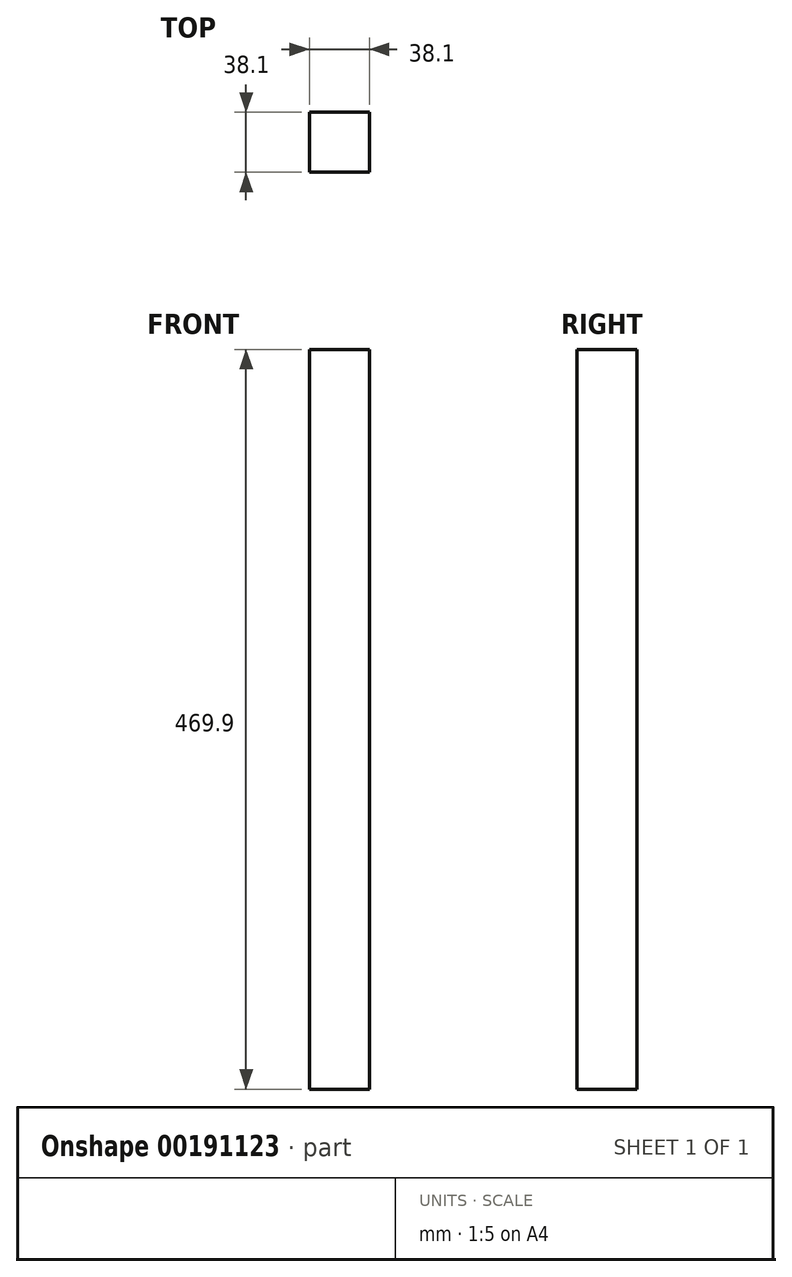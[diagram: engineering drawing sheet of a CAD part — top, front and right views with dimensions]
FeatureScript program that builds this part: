
annotation { "Feature Type Name" : "Feature", "Feature Type Description" : "" }
export const myFeature = defineFeature(function(context is Context, id is Id, definition is map)
    precondition{}
    {
        {
            var Q0;
            Q0=qCreatedBy(makeId("Top.planeOp"),FACE);
            var sketch = newSketch(context, id + "F0", { "sketchPlane" : qUnion([Q0])});
            skLineSegment(sketch, "E0.bottom", {"start": v(19.05, 19.05) * mm, "end": v(-19.05, 19.05) * mm});
            skLineSegment(sketch, "E0.top", {"start": v(19.05, -19.05) * mm, "end": v(-19.05, -19.05) * mm});
            skLineSegment(sketch, "E0.left", {"start": v(19.05, 19.05) * mm, "end": v(19.05, -19.05) * mm});
            skLineSegment(sketch, "E0.right", {"start": v(-19.05, 19.05) * mm, "end": v(-19.05, -19.05) * mm});
            skPoint(sketch, "E0.middle", {"position": v(0, 0) * mm});
            skSolve(sketch);
        }
        {
            var Q0;
            Q0 = qSketchRegion(id + "F0", true);
            extrude(context, id + "F1", {"entities" : qUnion([Q0]), "endBound" : BoundingType.SYMMETRIC, "depth" : 469.9 * mm});
        }
    });
